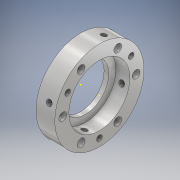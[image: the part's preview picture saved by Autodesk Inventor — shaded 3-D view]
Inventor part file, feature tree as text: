
AUTODESK INVENTOR PART (.ipt)
format: ipt  version: 2017.3 (Build 213256000, 256)  size: 191,488 bytes
history: native  units: mm
features: sketch x16, plane x8, extrude x5, hole x5, other x1
ambient origin geometry x8: Origin, YZ Plane, XZ Plane, XY Plane, X Axis, Y Axis, Z Axis, Center Point
bodies: Solid1 (feature_tree)
feature tree (35):
  extrude  "Extrusion1"  Depth=1.0mm TaperAngle=0.0deg
  sketch  "Sketch2"  dims[d3=1.0mm d4=1.67mm]
  sketch  "Sketch3"  dims[d5=1.67mm d6=1.67mm]
  extrude  "Extrusion2"  Depth=1.0mm
  extrude  "Extrusion3"  Depth=1.67mm
  extrude  "Extrusion4"  Depth=1.67mm
  extrude  "Extrusion5"  Depth=3.0mm TaperAngle=0.0deg
  plane  "Work Plane1"
  plane  "Work Plane2"
  plane  "Work Plane3"
  plane  "Work Plane4"
  plane  "Work Plane5"
  plane  "Work Plane6"
  plane  "Work Plane7"
  plane  "Work Plane8"
  sketch  "Sketch7"  dims[d15=4.0mm d16=0.0mm d17=13.0mm]
  sketch  "Sketch8"  dims[d18=3.0mm d19=0.0mm]
  sketch  "Sketch9"  dims[d20=15.0deg d21=90.0deg d22=-9.5mm d23=9.5mm d24=-9.5mm d25=9.5mm]
  sketch  "Sketch10"  dims[d54=1.221mm d55=3.2mm d56=4.0mm d57=2.0mm d58=90.0deg d59=3.2mm d60=20.594885mm]
  sketch  "Sketch12"  dims[d61=1.221mm d62=3.2mm d63=4.0mm d64=2.0mm d65=90.0deg d66=3.2mm d67=20.594885mm]
  sketch  "Sketch13"  dims[d68=1.221mm d69=3.2mm d70=4.0mm d71=2.0mm d72=90.0deg d73=3.2mm d74=20.594885mm]
  sketch  "Sketch14"  dims[d75=1.221mm d76=3.2mm d77=4.0mm d78=2.0mm d79=90.0deg d80=3.2mm d81=20.594885mm]
  sketch  "Sketch15"  dims[d82=1.221mm d83=2.0mm d84=4.0mm d85=2.0mm d86=90.0deg d87=2.0mm d88=20.594885mm]
  sketch  "Sketch16"
  hole  "Hole5"  [1 undecoded]
  hole  "Hole6"  [1 undecoded]
  hole  "Hole7"  [1 undecoded]
  hole  "Hole8"  [1 undecoded]
  hole  "Hole9"  [1 undecoded]
  sketch  "Sketch1"  dims[d0=19.0mm d1=1.0mm d2=0.0mm]
  sketch  "Sketch4"  dims[d7=1.67mm d8=1.67mm]
  sketch  "Sketch5"  dims[d9=1.67mm d10=3.0mm d11=0.0mm]
  sketch  "Sketch6"  dims[d12=4.0mm d13=0.0mm d14=10.0mm]
  other  "Work Axis1"
  sketch  "Sketch17"
note: 5 required parameter values undecoded (feature->parameter linkage not recoverable at this tier; creation-order binding heuristic only, values carry confidence <= 0.55)
